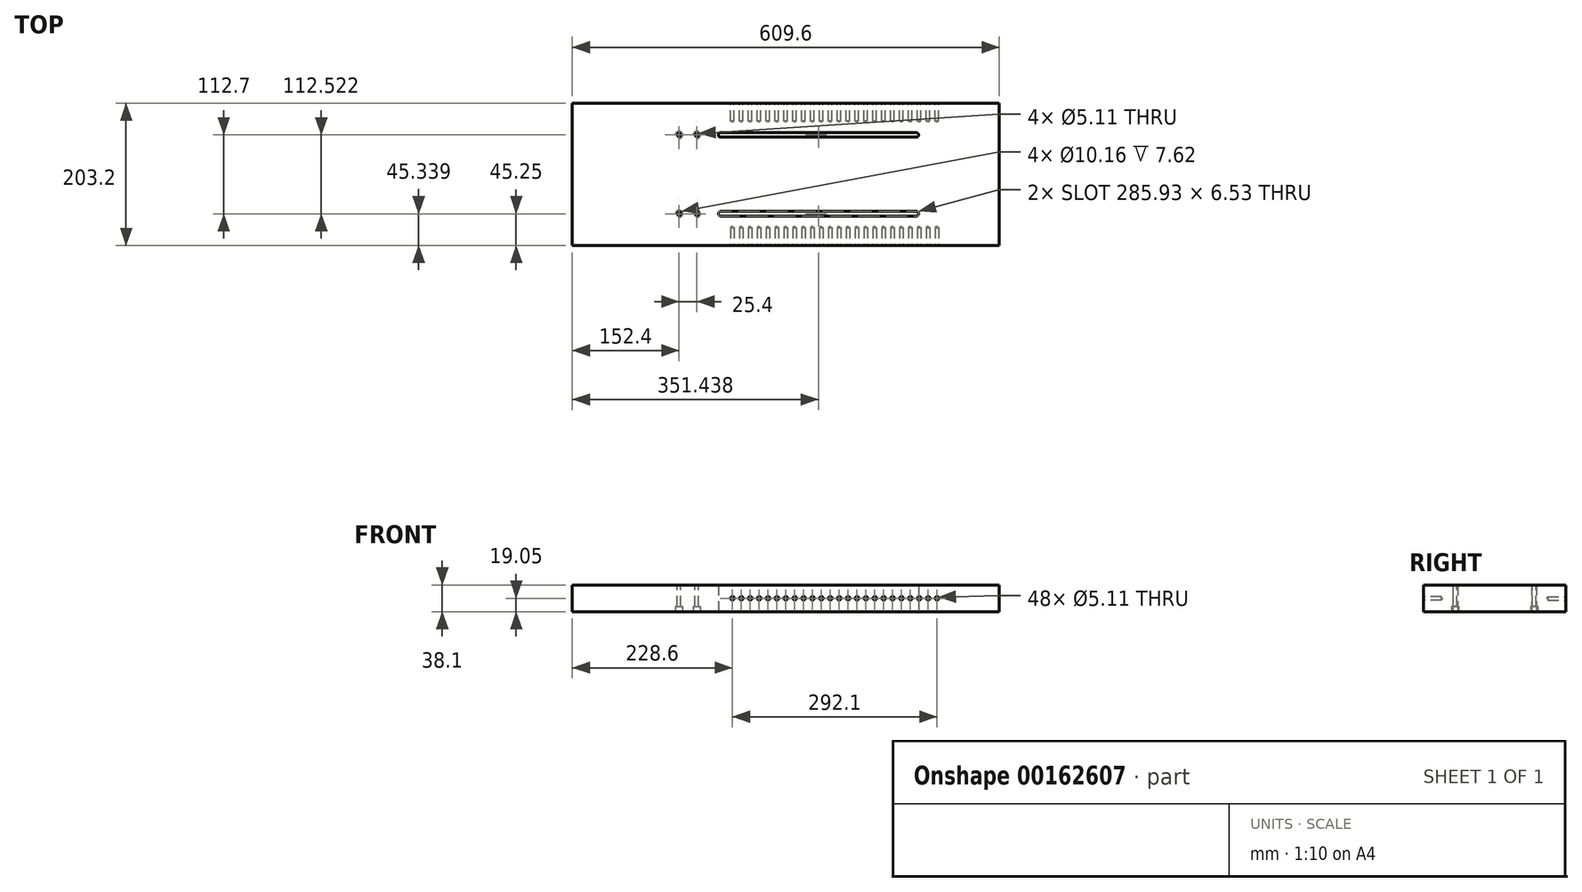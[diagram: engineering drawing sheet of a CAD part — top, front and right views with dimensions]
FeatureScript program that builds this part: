
annotation { "Feature Type Name" : "Feature", "Feature Type Description" : "" }
export const myFeature = defineFeature(function(context is Context, id is Id, definition is map)
    precondition{}
    {
        {
            var Q0;
            Q0=qCreatedBy(makeId("Front.planeOp"),FACE);
            var sketch = newSketch(context, id + "F0", { "sketchPlane" : qUnion([Q0])});
            skLineSegment(sketch, "E0.bottom", {"start": v(0, 0) * mm, "end": v(609.6, 0) * mm});
            skLineSegment(sketch, "E0.top", {"start": v(0, 38.1) * mm, "end": v(609.6, 38.1) * mm});
            skLineSegment(sketch, "E0.left", {"start": v(0, 0) * mm, "end": v(0, 38.1) * mm});
            skLineSegment(sketch, "E0.right", {"start": v(609.6, 0) * mm, "end": v(609.6, 38.1) * mm});
            skSolve(sketch);
        }
        {
            var Q0;
            Q0=makeQuery(id+"F0.imprint","IMPRINT",FACE,{"disambiguationData":[TD([[makeQuery(id+"F0.imprint","IMPRINT",EDGE,{"derivedFrom":sQuery(id+"F0.wireOp",EDGE,"E0.bottom")}),1.0]])]});
            extrude(context, id + "F1", {"entities" : qUnion([Q0]), "oppositeDirection" : true, "depth" : 203.2 * mm});
        }
        {
            var Q0;
            Q0=makeQuery(id+"F1.opExtrude","SWEPT_FACE",FACE,{"disambiguationData":[OSD([sQuery(id+"F0.wireOp",EDGE,"E0.top")])]});
            var sketch = newSketch(context, id + "F2", { "sketchPlane" : qUnion([Q0])});
            skLineSegment(sketch, "E1", {"start": v(-54.58, 101.6) * mm, "end": v(629.84, 101.6) * mm});
            skCircle(sketch, "E2", {"center": v(152.4, 157.95) * mm, "radius": 2.55 * mm});
            skCircle(sketch, "E3.1.0.0", {"center": v(177.8, 157.95) * mm, "radius": 2.55 * mm});
            skLineSegment(sketch, "E3.direction1", {"start": v(152.4, 157.95) * mm, "end": v(177.8, 157.95) * mm, "construction": true});
            skCircle(sketch, "E4", {"center": v(152.4, 45.25) * mm, "radius": 2.55 * mm});
            skCircle(sketch, "E5", {"center": v(177.8, 45.25) * mm, "radius": 2.55 * mm});
            skSolve(sketch);
        }
        {
            var Q0;
            Q0=sQuery(id+"F2.wireOp",VERTEX,"E2.center");
            var Q1;
            Q1=sQuery(id+"F2.wireOp",VERTEX,"E3.1.0.0.center");
            var Q2;
            Q2=sQuery(id+"F2.wireOp",VERTEX,"E4.center");
            var Q3;
            Q3=sQuery(id+"F2.wireOp",VERTEX,"E5.center");
            var Q4;
            Q4=makeQuery(id+"F1.opExtrude","SWEPT_BODY",BODY,{"disambiguationData":[OSD([sQuery(id+"F0.wireOp",EDGE,"E0.bottom"),sQuery(id+"F0.wireOp",EDGE,"E0.top"),sQuery(id+"F0.wireOp",EDGE,"E0.left"),sQuery(id+"F0.wireOp",EDGE,"E0.right")])]});
            hole(context, id + "F3", {"style" : HoleStyle.SIMPLE, "endStyle" : HoleEndStyle.THROUGH, "holeDiameter" : 5.1 * mm, "locations" : qUnion([Q0, Q1, Q2, Q3]), "scope" : qUnion([Q4]), "isTappedThrough" : true});
        }
        {
            var Q0;
            Q0=makeQuery(id+"F1.opExtrude","CAP_FACE",FACE,{"disambiguationData":[OSD([sQuery(id+"F0.wireOp",EDGE,"E0.bottom"),sQuery(id+"F0.wireOp",EDGE,"E0.top"),sQuery(id+"F0.wireOp",EDGE,"E0.left"),sQuery(id+"F0.wireOp",EDGE,"E0.right")])],"isStart":true});
            var sketch = newSketch(context, id + "F4", { "sketchPlane" : qUnion([Q0])});
            skCircle(sketch, "E6", {"center": v(228.6, 19.05) * mm, "radius": 2.55 * mm});
            skCircle(sketch, "E7.1.0.0", {"center": v(241.3, 19.05) * mm, "radius": 2.55 * mm});
            skCircle(sketch, "E7.2.0.0", {"center": v(254, 19.05) * mm, "radius": 2.55 * mm});
            skCircle(sketch, "E7.3.0.0", {"center": v(266.7, 19.05) * mm, "radius": 2.55 * mm});
            skCircle(sketch, "E7.4.0.0", {"center": v(279.4, 19.05) * mm, "radius": 2.55 * mm});
            skCircle(sketch, "E7.5.0.0", {"center": v(292.1, 19.05) * mm, "radius": 2.55 * mm});
            skCircle(sketch, "E7.6.0.0", {"center": v(304.8, 19.05) * mm, "radius": 2.55 * mm});
            skCircle(sketch, "E7.7.0.0", {"center": v(317.5, 19.05) * mm, "radius": 2.55 * mm});
            skCircle(sketch, "E7.8.0.0", {"center": v(330.2, 19.05) * mm, "radius": 2.55 * mm});
            skCircle(sketch, "E7.9.0.0", {"center": v(342.9, 19.05) * mm, "radius": 2.55 * mm});
            skCircle(sketch, "E7.10.0.0", {"center": v(355.6, 19.05) * mm, "radius": 2.55 * mm});
            skCircle(sketch, "E7.11.0.0", {"center": v(368.3, 19.05) * mm, "radius": 2.55 * mm});
            skLineSegment(sketch, "E7.direction1", {"start": v(228.6, 19.05) * mm, "end": v(241.3, 19.05) * mm, "construction": true});
            skCircle(sketch, "E8.0.12.0", {"center": v(381, 19.05) * mm, "radius": 2.55 * mm});
            skCircle(sketch, "E8.0.13.0", {"center": v(393.7, 19.05) * mm, "radius": 2.55 * mm});
            skCircle(sketch, "E8.0.14.0", {"center": v(406.4, 19.05) * mm, "radius": 2.55 * mm});
            skCircle(sketch, "E8.0.15.0", {"center": v(419.1, 19.05) * mm, "radius": 2.55 * mm});
            skCircle(sketch, "E8.0.16.0", {"center": v(431.8, 19.05) * mm, "radius": 2.55 * mm});
            skCircle(sketch, "E8.0.17.0", {"center": v(444.5, 19.05) * mm, "radius": 2.55 * mm});
            skCircle(sketch, "E8.0.18.0", {"center": v(457.2, 19.05) * mm, "radius": 2.55 * mm});
            skCircle(sketch, "E8.0.19.0", {"center": v(469.9, 19.05) * mm, "radius": 2.55 * mm});
            skCircle(sketch, "E8.0.20.0", {"center": v(482.6, 19.05) * mm, "radius": 2.55 * mm});
            skCircle(sketch, "E8.0.21.0", {"center": v(495.3, 19.05) * mm, "radius": 2.55 * mm});
            skCircle(sketch, "E8.0.22.0", {"center": v(508, 19.05) * mm, "radius": 2.55 * mm});
            skCircle(sketch, "E8.0.23.0", {"center": v(520.7, 19.05) * mm, "radius": 2.55 * mm});
            skSolve(sketch);
        }
        {
            var Q0;
            Q0=sQuery(id+"F4.wireOp",VERTEX,"E6.center");
            var Q1;
            Q1=sQuery(id+"F4.wireOp",VERTEX,"E7.1.0.0.center");
            var Q2;
            Q2=sQuery(id+"F4.wireOp",VERTEX,"E7.2.0.0.center");
            var Q3;
            Q3=sQuery(id+"F4.wireOp",VERTEX,"E7.3.0.0.center");
            var Q4;
            Q4=sQuery(id+"F4.wireOp",VERTEX,"E7.4.0.0.center");
            var Q5;
            Q5=sQuery(id+"F4.wireOp",VERTEX,"E7.5.0.0.center");
            var Q6;
            Q6=sQuery(id+"F4.wireOp",VERTEX,"E7.6.0.0.center");
            var Q7;
            Q7=sQuery(id+"F4.wireOp",VERTEX,"E7.7.0.0.center");
            var Q8;
            Q8=sQuery(id+"F4.wireOp",VERTEX,"E7.8.0.0.center");
            var Q9;
            Q9=sQuery(id+"F4.wireOp",VERTEX,"E7.9.0.0.center");
            var Q10;
            Q10=sQuery(id+"F4.wireOp",VERTEX,"E7.10.0.0.center");
            var Q11;
            Q11=sQuery(id+"F4.wireOp",VERTEX,"E7.11.0.0.center");
            var Q12;
            Q12=sQuery(id+"F4.wireOp",VERTEX,"E8.0.12.0.center");
            var Q13;
            Q13=sQuery(id+"F4.wireOp",VERTEX,"E8.0.13.0.center");
            var Q14;
            Q14=sQuery(id+"F4.wireOp",VERTEX,"E8.0.14.0.center");
            var Q15;
            Q15=sQuery(id+"F4.wireOp",VERTEX,"E8.0.15.0.center");
            var Q16;
            Q16=sQuery(id+"F4.wireOp",VERTEX,"E8.0.16.0.center");
            var Q17;
            Q17=sQuery(id+"F4.wireOp",VERTEX,"E8.0.17.0.center");
            var Q18;
            Q18=sQuery(id+"F4.wireOp",VERTEX,"E8.0.18.0.center");
            var Q19;
            Q19=sQuery(id+"F4.wireOp",VERTEX,"E8.0.19.0.center");
            var Q20;
            Q20=sQuery(id+"F4.wireOp",VERTEX,"E8.0.20.0.center");
            var Q21;
            Q21=sQuery(id+"F4.wireOp",VERTEX,"E8.0.21.0.center");
            var Q22;
            Q22=sQuery(id+"F4.wireOp",VERTEX,"E8.0.22.0.center");
            var Q23;
            Q23=sQuery(id+"F4.wireOp",VERTEX,"E8.0.23.0.center");
            var Q24;
            Q24=makeQuery(id+"F1.opExtrude","SWEPT_BODY",BODY,{"disambiguationData":[OSD([sQuery(id+"F0.wireOp",EDGE,"E0.bottom"),sQuery(id+"F0.wireOp",EDGE,"E0.top"),sQuery(id+"F0.wireOp",EDGE,"E0.left"),sQuery(id+"F0.wireOp",EDGE,"E0.right")])]});
            hole(context, id + "F5", {"style" : HoleStyle.SIMPLE, "endStyle" : HoleEndStyle.BLIND, "holeDiameter" : 5.1 * mm, "holeDepth" : 25.4 * mm, "locations" : qUnion([Q0, Q1, Q2, Q3, Q4, Q5, Q6, Q7, Q8, Q9, Q10, Q11, Q12, Q13, Q14, Q15, Q16, Q17, Q18, Q19, Q20, Q21, Q22, Q23]), "scope" : qUnion([Q24])});
        }
        {
            var Q0;
            Q0=makeQuery(id+"F1.opExtrude","CAP_FACE",FACE,{"disambiguationData":[OSD([sQuery(id+"F0.wireOp",EDGE,"E0.bottom"),sQuery(id+"F0.wireOp",EDGE,"E0.top"),sQuery(id+"F0.wireOp",EDGE,"E0.left"),sQuery(id+"F0.wireOp",EDGE,"E0.right")])],"isStart":false});
            var sketch = newSketch(context, id + "F6", { "sketchPlane" : qUnion([Q0])});
            skCircle(sketch, "E9", {"center": v(-228.6, 19.05) * mm, "radius": 2.55 * mm});
            skCircle(sketch, "E10.1.0.0", {"center": v(-241.3, 19.05) * mm, "radius": 2.55 * mm});
            skCircle(sketch, "E10.2.0.0", {"center": v(-254, 19.05) * mm, "radius": 2.55 * mm});
            skCircle(sketch, "E10.3.0.0", {"center": v(-266.7, 19.05) * mm, "radius": 2.55 * mm});
            skCircle(sketch, "E10.4.0.0", {"center": v(-279.4, 19.05) * mm, "radius": 2.55 * mm});
            skCircle(sketch, "E10.5.0.0", {"center": v(-292.1, 19.05) * mm, "radius": 2.55 * mm});
            skCircle(sketch, "E10.6.0.0", {"center": v(-304.8, 19.05) * mm, "radius": 2.55 * mm});
            skCircle(sketch, "E10.7.0.0", {"center": v(-317.5, 19.05) * mm, "radius": 2.55 * mm});
            skCircle(sketch, "E10.8.0.0", {"center": v(-330.2, 19.05) * mm, "radius": 2.55 * mm});
            skCircle(sketch, "E10.9.0.0", {"center": v(-342.9, 19.05) * mm, "radius": 2.55 * mm});
            skCircle(sketch, "E10.10.0.0", {"center": v(-355.6, 19.05) * mm, "radius": 2.55 * mm});
            skCircle(sketch, "E10.11.0.0", {"center": v(-368.3, 19.05) * mm, "radius": 2.55 * mm});
            skCircle(sketch, "E10.12.0.0", {"center": v(-381, 19.05) * mm, "radius": 2.55 * mm});
            skCircle(sketch, "E10.13.0.0", {"center": v(-393.7, 19.05) * mm, "radius": 2.55 * mm});
            skCircle(sketch, "E10.14.0.0", {"center": v(-406.4, 19.05) * mm, "radius": 2.55 * mm});
            skCircle(sketch, "E10.15.0.0", {"center": v(-419.1, 19.05) * mm, "radius": 2.55 * mm});
            skCircle(sketch, "E10.16.0.0", {"center": v(-431.8, 19.05) * mm, "radius": 2.55 * mm});
            skCircle(sketch, "E10.17.0.0", {"center": v(-444.5, 19.05) * mm, "radius": 2.55 * mm});
            skCircle(sketch, "E10.18.0.0", {"center": v(-457.2, 19.05) * mm, "radius": 2.55 * mm});
            skCircle(sketch, "E10.19.0.0", {"center": v(-469.9, 19.05) * mm, "radius": 2.55 * mm});
            skCircle(sketch, "E10.20.0.0", {"center": v(-482.6, 19.05) * mm, "radius": 2.55 * mm});
            skCircle(sketch, "E10.21.0.0", {"center": v(-495.3, 19.05) * mm, "radius": 2.55 * mm});
            skCircle(sketch, "E10.22.0.0", {"center": v(-508, 19.05) * mm, "radius": 2.55 * mm});
            skCircle(sketch, "E10.23.0.0", {"center": v(-520.7, 19.05) * mm, "radius": 2.55 * mm});
            skLineSegment(sketch, "E10.direction1", {"start": v(-228.6, 19.05) * mm, "end": v(-241.3, 19.05) * mm, "construction": true});
            skSolve(sketch);
        }
        {
            var Q0;
            Q0=sQuery(id+"F6.wireOp",VERTEX,"E9.center");
            var Q1;
            Q1=sQuery(id+"F6.wireOp",VERTEX,"E10.1.0.0.center");
            var Q2;
            Q2=sQuery(id+"F6.wireOp",VERTEX,"E10.2.0.0.center");
            var Q3;
            Q3=sQuery(id+"F6.wireOp",VERTEX,"E10.3.0.0.center");
            var Q4;
            Q4=sQuery(id+"F6.wireOp",VERTEX,"E10.4.0.0.center");
            var Q5;
            Q5=sQuery(id+"F6.wireOp",VERTEX,"E10.5.0.0.center");
            var Q6;
            Q6=sQuery(id+"F6.wireOp",VERTEX,"E10.6.0.0.center");
            var Q7;
            Q7=sQuery(id+"F6.wireOp",VERTEX,"E10.7.0.0.center");
            var Q8;
            Q8=sQuery(id+"F6.wireOp",VERTEX,"E10.8.0.0.center");
            var Q9;
            Q9=sQuery(id+"F6.wireOp",VERTEX,"E10.9.0.0.center");
            var Q10;
            Q10=sQuery(id+"F6.wireOp",VERTEX,"E10.10.0.0.center");
            var Q11;
            Q11=sQuery(id+"F6.wireOp",VERTEX,"E10.11.0.0.center");
            var Q12;
            Q12=sQuery(id+"F6.wireOp",VERTEX,"E10.12.0.0.center");
            var Q13;
            Q13=sQuery(id+"F6.wireOp",VERTEX,"E10.13.0.0.center");
            var Q14;
            Q14=sQuery(id+"F6.wireOp",VERTEX,"E10.14.0.0.center");
            var Q15;
            Q15=sQuery(id+"F6.wireOp",VERTEX,"E10.15.0.0.center");
            var Q16;
            Q16=sQuery(id+"F6.wireOp",VERTEX,"E10.16.0.0.center");
            var Q17;
            Q17=sQuery(id+"F6.wireOp",VERTEX,"E10.17.0.0.center");
            var Q18;
            Q18=sQuery(id+"F6.wireOp",VERTEX,"E10.18.0.0.center");
            var Q19;
            Q19=sQuery(id+"F6.wireOp",VERTEX,"E10.19.0.0.center");
            var Q20;
            Q20=sQuery(id+"F6.wireOp",VERTEX,"E10.20.0.0.center");
            var Q21;
            Q21=sQuery(id+"F6.wireOp",VERTEX,"E10.21.0.0.center");
            var Q22;
            Q22=sQuery(id+"F6.wireOp",VERTEX,"E10.22.0.0.center");
            var Q23;
            Q23=sQuery(id+"F6.wireOp",VERTEX,"E10.23.0.0.center");
            var Q24;
            Q24=makeQuery(id+"F1.opExtrude","SWEPT_BODY",BODY,{"disambiguationData":[OSD([sQuery(id+"F0.wireOp",EDGE,"E0.bottom"),sQuery(id+"F0.wireOp",EDGE,"E0.top"),sQuery(id+"F0.wireOp",EDGE,"E0.left"),sQuery(id+"F0.wireOp",EDGE,"E0.right")])]});
            hole(context, id + "F7", {"style" : HoleStyle.SIMPLE, "endStyle" : HoleEndStyle.BLIND, "holeDiameter" : 5.1 * mm, "holeDepth" : 25.4 * mm, "locations" : qUnion([Q0, Q1, Q2, Q3, Q4, Q5, Q6, Q7, Q8, Q9, Q10, Q11, Q12, Q13, Q14, Q15, Q16, Q17, Q18, Q19, Q20, Q21, Q22, Q23]), "scope" : qUnion([Q24])});
        }
        {
            var Q0;
            Q0=makeQuery(id+"F1.opExtrude","SWEPT_FACE",FACE,{"disambiguationData":[OSD([sQuery(id+"F0.wireOp",EDGE,"E0.bottom")])]});
            var sketch = newSketch(context, id + "F8", { "sketchPlane" : qUnion([Q0])});
            skCircle(sketch, "E11", {"center": v(177.8, -157.95) * mm, "radius": 5.08 * mm});
            skCircle(sketch, "E12", {"center": v(152.4, -157.95) * mm, "radius": 5.08 * mm});
            skCircle(sketch, "E13", {"center": v(177.8, -45.25) * mm, "radius": 5.08 * mm});
            skCircle(sketch, "E14", {"center": v(152.4, -45.25) * mm, "radius": 5.08 * mm});
            skSolve(sketch);
        }
        {
            var Q0;
            Q0 = qSketchRegion(id + "F8", true);
            extrude(context, id + "F9", {"entities" : qUnion([Q0]), "operationType" : NewBodyOperationType.REMOVE, "oppositeDirection" : true, "depth" : 7.62 * mm});
        }
        {
            var Q0;
            Q0=makeQuery(id+"F1.opExtrude","SWEPT_FACE",FACE,{"disambiguationData":[OSD([sQuery(id+"F0.wireOp",EDGE,"E0.bottom")])]});
            var sketch = newSketch(context, id + "F10", { "sketchPlane" : qUnion([Q0])});
            skSolve(sketch);
        }
        {
            var Q0;
            {var subQ0=sQuery(id+"F0.wireOp",EDGE,"E0.bottom");Q0=makeQuery(id+"F10.imprint","IMPRINT",FACE,{"disambiguationData":[TD([[makeQuery(id+"F10.imprint","IMPRINT",EDGE,{"derivedFrom":makeQuery(id+"F1.opExtrude","CAP_EDGE",EDGE,{"disambiguationData":[OSD([subQ0])],"isStart":true})}),-1.0]])]});}
            var sketch = newSketch(context, id + "F11", { "sketchPlane" : qUnion([Q0])});
            skLineSegment(sketch, "E15.bottom", {"start": v(211.74, -161.12) * mm, "end": v(491.14, -161.12) * mm});
            skLineSegment(sketch, "E15.top", {"start": v(211.74, -154.6) * mm, "end": v(491.14, -154.6) * mm});
            skArc(sketch, "E16", {"start": v(211.74, -161.12) * mm, "mid": v(208.47, -157.86) * mm, "end": v(211.74, -154.6) * mm});
            skArc(sketch, "E17", {"start": v(491.14, -154.6) * mm, "mid": v(494.4, -157.86) * mm, "end": v(491.14, -161.12) * mm});
            skLineSegment(sketch, "E18", {"start": v(0, -101.6) * mm, "end": v(611.18, -101.6) * mm});
            skLineSegment(sketch, "E19.MirrorCS", {"start": v(211.74, -48.6) * mm, "end": v(491.14, -48.6) * mm});
            skArc(sketch, "E20.MirrorCS", {"start": v(211.74, -42.08) * mm, "mid": v(208.47, -45.34) * mm, "end": v(211.74, -48.6) * mm});
            skLineSegment(sketch, "E21.MirrorCS", {"start": v(211.74, -42.08) * mm, "end": v(491.14, -42.08) * mm});
            skArc(sketch, "E22.MirrorCS", {"start": v(491.14, -48.6) * mm, "mid": v(494.4, -45.34) * mm, "end": v(491.14, -42.08) * mm});
            skLineSegment(sketch, "E23.bottom", {"start": v(211.74, -163.66) * mm, "end": v(491.14, -163.66) * mm});
            skLineSegment(sketch, "E23.top", {"start": v(211.74, -152.23) * mm, "end": v(491.14, -152.23) * mm});
            skLineSegment(sketch, "E23.left", {"start": v(211.74, -157.95) * mm, "end": v(211.74, -157.86) * mm});
            skArc(sketch, "E24", {"start": v(491.14, -152.23) * mm, "mid": v(496.85, -157.95) * mm, "end": v(491.14, -163.66) * mm});
            skArc(sketch, "E25", {"start": v(211.74, -152.23) * mm, "mid": v(206.02, -157.95) * mm, "end": v(211.74, -163.66) * mm});
            skLineSegment(sketch, "E26.trimOffspring", {"start": v(491.14, -157.95) * mm, "end": v(491.14, -157.86) * mm});
            skArc(sketch, "E27.MirrorCS", {"start": v(211.74, -50.97) * mm, "mid": v(206.02, -45.25) * mm, "end": v(211.74, -39.54) * mm});
            skLineSegment(sketch, "E28.MirrorCS", {"start": v(211.74, -50.97) * mm, "end": v(491.14, -50.97) * mm});
            skLineSegment(sketch, "E29.MirrorCS", {"start": v(211.74, -39.54) * mm, "end": v(491.14, -39.54) * mm});
            skArc(sketch, "E30.MirrorCS", {"start": v(491.14, -50.97) * mm, "mid": v(496.85, -45.25) * mm, "end": v(491.14, -39.54) * mm});
            skSolve(sketch);
        }
        {
            var Q0;
            Q0=makeQuery(id+"F11.imprint","IMPRINT",FACE,{"disambiguationData":[TD([[makeQuery(id+"F11.imprint","IMPRINT",EDGE,{"derivedFrom":sQuery(id+"F11.wireOp",EDGE,"E15.bottom")}),1.0]])]});
            var Q1;
            Q1=makeQuery(id+"F11.imprint","IMPRINT",FACE,{"disambiguationData":[TD([[makeQuery(id+"F11.imprint","IMPRINT",EDGE,{"derivedFrom":sQuery(id+"F11.wireOp",EDGE,"E19.MirrorCS")}),1.0]])]});
            extrude(context, id + "F12", {"entities" : qUnion([Q0, Q1]), "operationType" : NewBodyOperationType.REMOVE, "endBound" : BoundingType.THROUGH_ALL, "oppositeDirection" : true, "depth" : 25.4 * mm});
        }
        {
            var Q0;
            Q0=sQuery(id+"F11.wireOp",EDGE,"E23.bottom");
            var Q1;
            Q1=sQuery(id+"F11.wireOp",EDGE,"E25");
            var Q2;
            Q2=sQuery(id+"F11.wireOp",EDGE,"E23.top");
            var Q3;
            Q3=sQuery(id+"F11.wireOp",EDGE,"E28.MirrorCS");
            var Q4;
            Q4=sQuery(id+"F11.wireOp",EDGE,"E27.MirrorCS");
            var Q5;
            Q5=sQuery(id+"F11.wireOp",EDGE,"E29.MirrorCS");
            var Q6;
            Q6=sQuery(id+"F11.wireOp",EDGE,"E24");
            var Q7;
            Q7=sQuery(id+"F11.wireOp",EDGE,"E30.MirrorCS");
            extrude(context, id + "F13", {"bodyType" : ToolBodyType.SURFACE, "surfaceEntities" : qUnion([Q0, Q1, Q2, Q3, Q4, Q5, Q6, Q7]), "depth" : 7.62 * mm});
        }
    });
